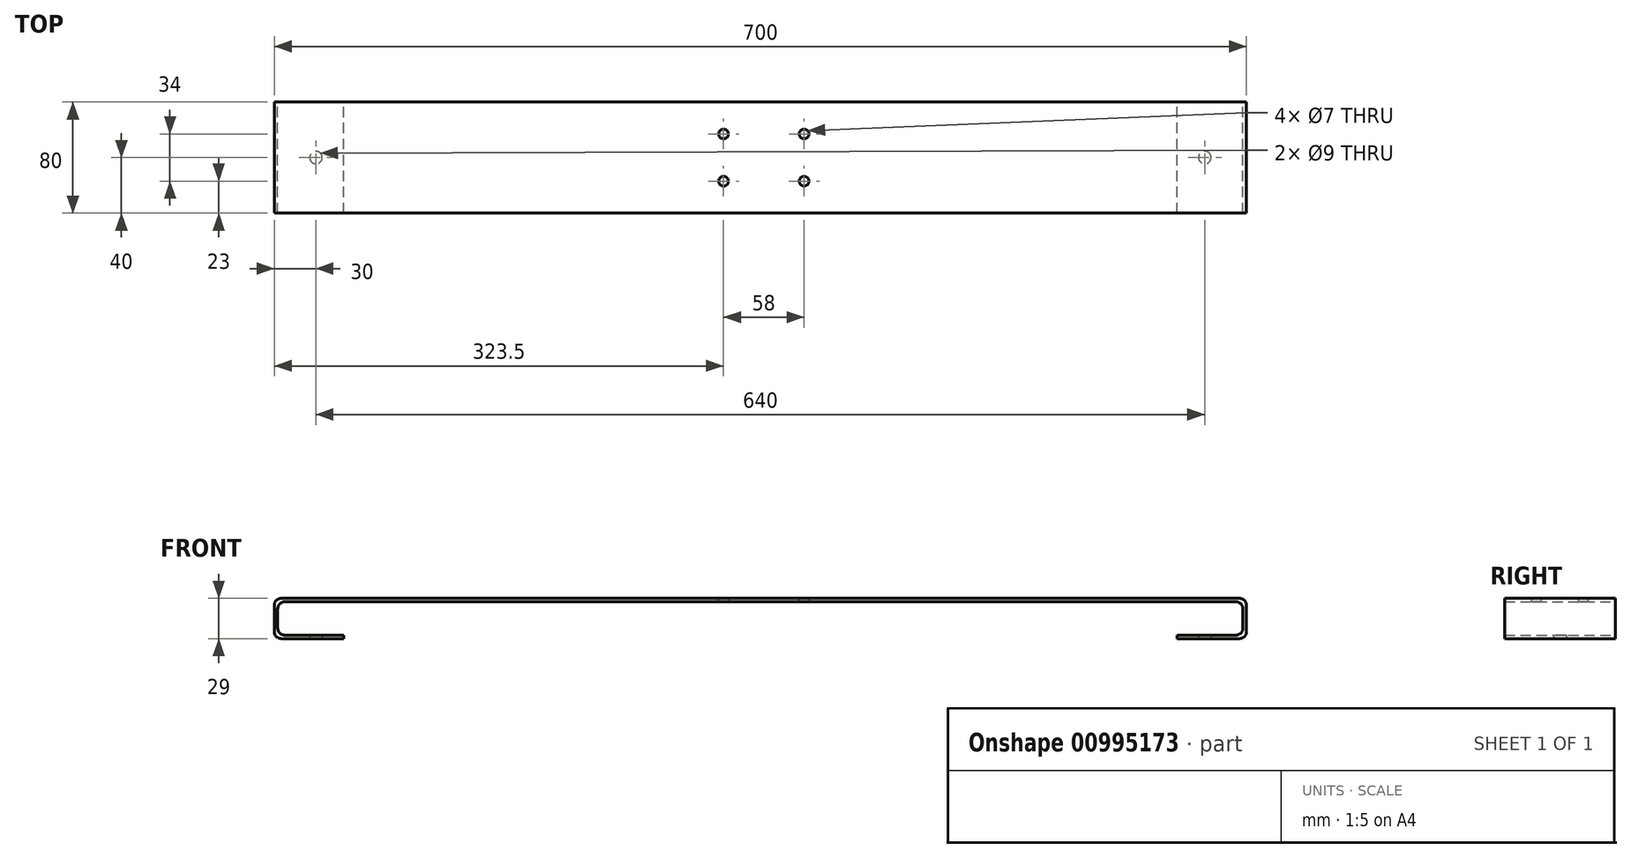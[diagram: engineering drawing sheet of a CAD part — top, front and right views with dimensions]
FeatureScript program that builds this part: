
annotation { "Feature Type Name" : "Feature", "Feature Type Description" : "" }
export const myFeature = defineFeature(function(context is Context, id is Id, definition is map)
    precondition{}
    {
        {
            var Q0;
            Q0=qCreatedBy(makeId("Front.planeOp"),FACE);
            var sketch = newSketch(context, id + "F0", { "sketchPlane" : qUnion([Q0])});
            skLineSegment(sketch, "E0", {"start": v(0, 0) * mm, "end": v(50, 0) * mm});
            skLineSegment(sketch, "E1", {"start": v(0, 0) * mm, "end": v(0, 29) * mm});
            skLineSegment(sketch, "E2", {"start": v(0, 29) * mm, "end": v(700, 29) * mm});
            skLineSegment(sketch, "E3", {"start": v(700, 29) * mm, "end": v(700, 0) * mm});
            skLineSegment(sketch, "E4", {"start": v(700, 0) * mm, "end": v(650, 0) * mm});
            skLineSegment(sketch, "E5.0", {"start": v(2.5, 2.5) * mm, "end": v(50, 2.5) * mm});
            skLineSegment(sketch, "E5.1", {"start": v(697.5, 2.5) * mm, "end": v(650, 2.5) * mm});
            skLineSegment(sketch, "E5.2", {"start": v(697.5, 26.5) * mm, "end": v(697.5, 2.5) * mm});
            skLineSegment(sketch, "E5.3", {"start": v(2.5, 26.5) * mm, "end": v(697.5, 26.5) * mm});
            skLineSegment(sketch, "E5.4", {"start": v(2.5, 2.5) * mm, "end": v(2.5, 26.5) * mm});
            skLineSegment(sketch, "E6", {"start": v(50, 2.5) * mm, "end": v(50, 0) * mm});
            skLineSegment(sketch, "E7", {"start": v(650, 2.5) * mm, "end": v(650, 0) * mm});
            skSolve(sketch);
        }
        {
            var Q0;
            Q0=qSketchRegion(id+"F0",true);
            extrude(context, id + "F1", {"entities" : qUnion([Q0]), "depth" : 80 * mm, "offsetDistance" : 25 * mm, "symmetric" : true});
        }
        {
            var Q0;
            Q0=makeQuery(id+"F1.opExtrude","SWEPT_FACE",FACE,{"disambiguationData":[OSD([sQuery(id+"F0.wireOp",EDGE,"E5.0")])]});
            var sketch = newSketch(context, id + "F2", { "sketchPlane" : qUnion([Q0])});
            skLineSegment(sketch, "E8", {"start": v(50, 0) * mm, "end": v(30, 0) * mm});
            skSolve(sketch);
        }
        {
            var Q0;
            Q0=makeQuery(id+"F1.opExtrude","SWEPT_FACE",FACE,{"disambiguationData":[OSD([sQuery(id+"F0.wireOp",EDGE,"E5.1")])]});
            var sketch = newSketch(context, id + "F3", { "sketchPlane" : qUnion([Q0])});
            skLineSegment(sketch, "E9", {"start": v(650, 0) * mm, "end": v(670, 0) * mm});
            skSolve(sketch);
        }
        {
            var Q0;
            Q0=sQuery(id+"F3.wireOp",VERTEX,"E9.end");
            var Q1;
            Q1=makeQuery(id+"F1.opExtrude","SWEPT_BODY",BODY,{"disambiguationData":[OSD([sQuery(id+"F0.wireOp",EDGE,"E0"),sQuery(id+"F0.wireOp",EDGE,"E1"),sQuery(id+"F0.wireOp",EDGE,"E2"),sQuery(id+"F0.wireOp",EDGE,"E3"),sQuery(id+"F0.wireOp",EDGE,"E4"),sQuery(id+"F0.wireOp",EDGE,"E5.0"),sQuery(id+"F0.wireOp",EDGE,"E5.1"),sQuery(id+"F0.wireOp",EDGE,"E5.2"),sQuery(id+"F0.wireOp",EDGE,"E5.3"),sQuery(id+"F0.wireOp",EDGE,"E5.4"),sQuery(id+"F0.wireOp",EDGE,"E6"),sQuery(id+"F0.wireOp",EDGE,"E7")])]});
            hole(context, id + "F4", {"style" : HoleStyle.SIMPLE, "endStyle" : HoleEndStyle.BLIND, "holeDiameter" : 9 * mm, "majorDiameter" : 5 * mm, "holeDepth" : 12 * mm, "isTappedThrough" : true, "tappedDepth" : 12 * mm, "tapClearance" : 3, "locations" : qUnion([Q0]), "scope" : qUnion([Q1]), "startStyle" : HoleStartStyle.PART});
        }
        {
            var Q0;
            Q0=sQuery(id+"F2.wireOp",VERTEX,"E8.end");
            var Q1;
            Q1=makeQuery(id+"F1.opExtrude","SWEPT_BODY",BODY,{"disambiguationData":[OSD([sQuery(id+"F0.wireOp",EDGE,"E0"),sQuery(id+"F0.wireOp",EDGE,"E1"),sQuery(id+"F0.wireOp",EDGE,"E2"),sQuery(id+"F0.wireOp",EDGE,"E3"),sQuery(id+"F0.wireOp",EDGE,"E4"),sQuery(id+"F0.wireOp",EDGE,"E5.0"),sQuery(id+"F0.wireOp",EDGE,"E5.1"),sQuery(id+"F0.wireOp",EDGE,"E5.2"),sQuery(id+"F0.wireOp",EDGE,"E5.3"),sQuery(id+"F0.wireOp",EDGE,"E5.4"),sQuery(id+"F0.wireOp",EDGE,"E6"),sQuery(id+"F0.wireOp",EDGE,"E7")])]});
            hole(context, id + "F5", {"style" : HoleStyle.SIMPLE, "endStyle" : HoleEndStyle.BLIND, "holeDiameter" : 9 * mm, "majorDiameter" : 5 * mm, "holeDepth" : 12 * mm, "isTappedThrough" : true, "tappedDepth" : 12 * mm, "tapClearance" : 3, "locations" : qUnion([Q0]), "scope" : qUnion([Q1]), "startStyle" : HoleStartStyle.PART});
        }
        {
            var Q0;
            Q0=makeQuery(id+"F1.opExtrude","SWEPT_FACE",FACE,{"disambiguationData":[OSD([sQuery(id+"F0.wireOp",EDGE,"E5.3")])]});
            var sketch = newSketch(context, id + "F6", { "sketchPlane" : qUnion([Q0])});
            skPoint(sketch, "E10.middle", {"position": v(247.5, 0) * mm});
            skLineSegment(sketch, "E11.bottom", {"start": v(381.5, -17) * mm, "end": v(323.5, -17) * mm});
            skLineSegment(sketch, "E11.top", {"start": v(381.5, 17) * mm, "end": v(323.5, 17) * mm});
            skLineSegment(sketch, "E11.left", {"start": v(381.5, -17) * mm, "end": v(381.5, 17) * mm});
            skLineSegment(sketch, "E11.right", {"start": v(323.5, -17) * mm, "end": v(323.5, 17) * mm});
            skPoint(sketch, "E11.middle", {"position": v(352.5, 0) * mm});
            skLineSegment(sketch, "E12", {"start": v(2.5, 0) * mm, "end": v(352.5, 0) * mm});
            skSolve(sketch);
        }
        {
            var Q0;
            Q0=sQuery(id+"F6.wireOp",VERTEX,"E10.left.start");
            var Q1;
            Q1=sQuery(id+"F6.wireOp",VERTEX,"E10.right.start");
            var Q2;
            Q2=sQuery(id+"F6.wireOp",VERTEX,"E10.right.end");
            var Q3;
            Q3=sQuery(id+"F6.wireOp",VERTEX,"E10.left.end");
            var Q4;
            Q4=sQuery(id+"F6.wireOp",VERTEX,"E11.bottom.start");
            var Q5;
            Q5=sQuery(id+"F6.wireOp",VERTEX,"E11.right.start");
            var Q6;
            Q6=sQuery(id+"F6.wireOp",VERTEX,"E11.right.end");
            var Q7;
            Q7=sQuery(id+"F6.wireOp",VERTEX,"E11.left.end");
            var Q8;
            Q8=makeQuery(id+"F1.opExtrude","SWEPT_BODY",BODY,{"disambiguationData":[OSD([sQuery(id+"F0.wireOp",EDGE,"E0"),sQuery(id+"F0.wireOp",EDGE,"E1"),sQuery(id+"F0.wireOp",EDGE,"E2"),sQuery(id+"F0.wireOp",EDGE,"E3"),sQuery(id+"F0.wireOp",EDGE,"E4"),sQuery(id+"F0.wireOp",EDGE,"E5.0"),sQuery(id+"F0.wireOp",EDGE,"E5.1"),sQuery(id+"F0.wireOp",EDGE,"E5.2"),sQuery(id+"F0.wireOp",EDGE,"E5.3"),sQuery(id+"F0.wireOp",EDGE,"E5.4"),sQuery(id+"F0.wireOp",EDGE,"E6"),sQuery(id+"F0.wireOp",EDGE,"E7")])]});
            hole(context, id + "F7", {"style" : HoleStyle.SIMPLE, "endStyle" : HoleEndStyle.THROUGH, "holeDiameter" : 7 * mm, "majorDiameter" : 5 * mm, "isTappedThrough" : true, "tappedDepth" : 12 * mm, "tapClearance" : 3, "locations" : qUnion([Q0, Q1, Q2, Q3, Q4, Q5, Q6, Q7]), "scope" : qUnion([Q8]), "startStyle" : HoleStartStyle.PART});
        }
        {
            var Q0;
            Q0=makeQuery(id+"F1.opExtrude","SWEPT_EDGE",EDGE,{"disambiguationData":[OSD([sQuery(id+"F0.wireOp",EDGE,"E1"),sQuery(id+"F0.wireOp",EDGE,"E2")])]});
            var Q1;
            Q1=makeQuery(id+"F1.opExtrude","SWEPT_EDGE",EDGE,{"disambiguationData":[OSD([sQuery(id+"F0.wireOp",EDGE,"E0"),sQuery(id+"F0.wireOp",EDGE,"E1")])]});
            var Q2;
            Q2=makeQuery(id+"F1.opExtrude","SWEPT_EDGE",EDGE,{"disambiguationData":[OSD([sQuery(id+"F0.wireOp",EDGE,"E2"),sQuery(id+"F0.wireOp",EDGE,"E3")])]});
            var Q3;
            Q3=makeQuery(id+"F1.opExtrude","SWEPT_EDGE",EDGE,{"disambiguationData":[OSD([sQuery(id+"F0.wireOp",EDGE,"E3"),sQuery(id+"F0.wireOp",EDGE,"E4")])]});
            var Q4;
            Q4=makeQuery(id+"F1.opExtrude","SWEPT_EDGE",EDGE,{"disambiguationData":[OSD([sQuery(id+"F0.wireOp",EDGE,"E5.0"),sQuery(id+"F0.wireOp",EDGE,"E5.4")])]});
            var Q5;
            Q5=makeQuery(id+"F1.opExtrude","SWEPT_EDGE",EDGE,{"disambiguationData":[OSD([sQuery(id+"F0.wireOp",EDGE,"E5.3"),sQuery(id+"F0.wireOp",EDGE,"E5.4")])]});
            var Q6;
            Q6=makeQuery(id+"F1.opExtrude","SWEPT_EDGE",EDGE,{"disambiguationData":[OSD([sQuery(id+"F0.wireOp",EDGE,"E5.1"),sQuery(id+"F0.wireOp",EDGE,"E5.2")])]});
            var Q7;
            Q7=makeQuery(id+"F1.opExtrude","SWEPT_EDGE",EDGE,{"disambiguationData":[OSD([sQuery(id+"F0.wireOp",EDGE,"E5.2"),sQuery(id+"F0.wireOp",EDGE,"E5.3")])]});
            fillet(context, id + "F8", {"entities" : qUnion([Q0, Q1, Q2, Q3, Q4, Q5, Q6, Q7]), "radius" : 5 * mm, "tangentPropagation" : true, "allowEdgeOverflow" : false});
        }
    });
